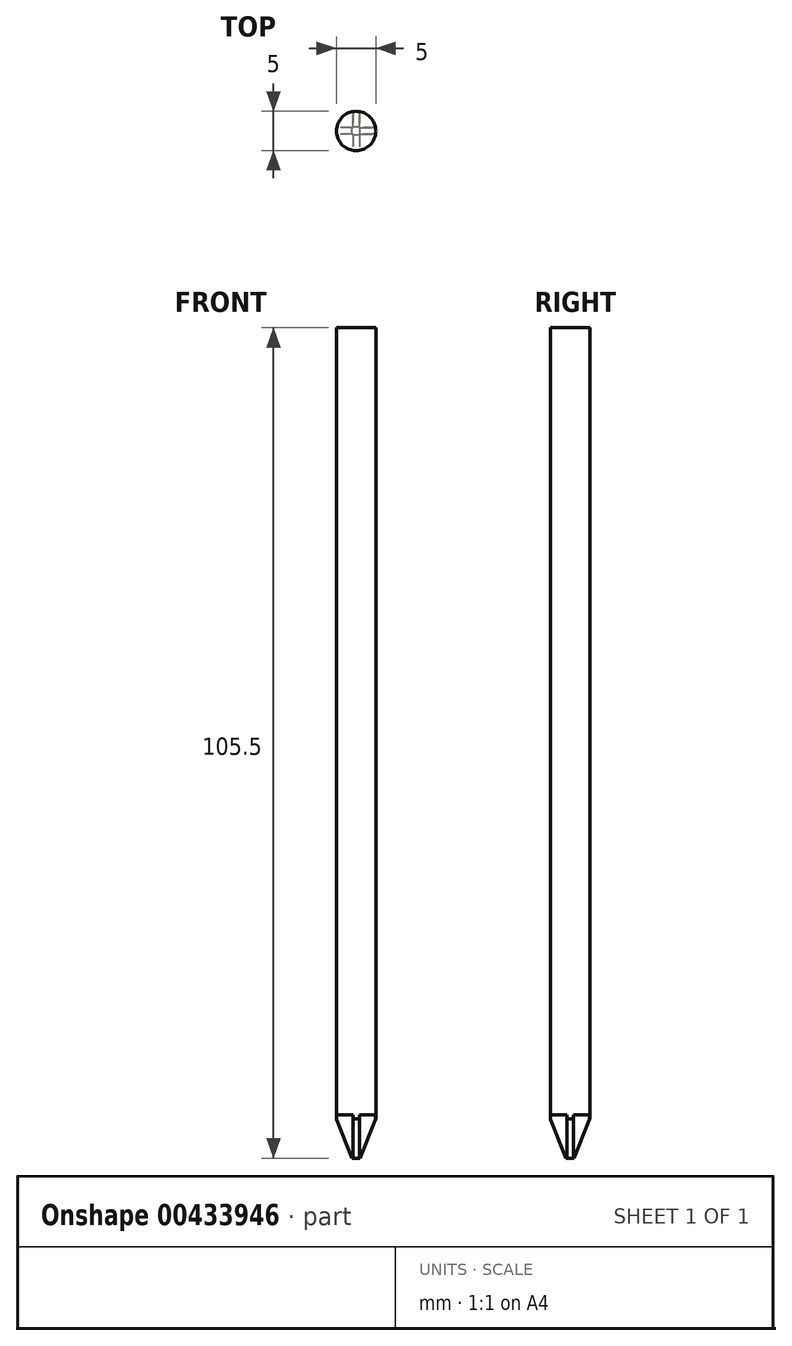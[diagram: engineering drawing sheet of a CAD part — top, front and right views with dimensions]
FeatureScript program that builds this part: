
annotation { "Feature Type Name" : "Feature", "Feature Type Description" : "" }
export const myFeature = defineFeature(function(context is Context, id is Id, definition is map)
    precondition{}
    {
        {
            var Q0;
            Q0=qCreatedBy(makeId("Front.planeOp"),FACE);
            var sketch = newSketch(context, id + "F0", { "sketchPlane" : qUnion([Q0])});
            skLineSegment(sketch, "E0", {"start": v(0, 0) * mm, "end": v(-10, 0) * mm});
            skLineSegment(sketch, "E1", {"start": v(-10, 0) * mm, "end": v(-10, 5) * mm});
            skLineSegment(sketch, "E2", {"start": v(-2.5, 0) * mm, "end": v(-2.5, -100) * mm});
            skLineSegment(sketch, "E3", {"start": v(-2.5, -100) * mm, "end": v(0, -100) * mm});
            skLineSegment(sketch, "E4", {"start": v(0, -100) * mm, "end": v(0, 80) * mm});
            skArc(sketch, "E5", {"start": v(0, 80) * mm, "mid": v(-5.14, 78.95) * mm, "end": v(-10, 77) * mm});
            skArc(sketch, "E6", {"start": v(-10, 5) * mm, "mid": v(-7.2, 7.32) * mm, "end": v(-5.04, 10.25) * mm});
            skArc(sketch, "E7", {"start": v(-10, 77) * mm, "mid": v(-10.59, 43.4) * mm, "end": v(-5.04, 10.25) * mm});
            skSolve(sketch);
        }
        {
            var Q0;
            {var subQ0=sQuery(id+"F0.wireOp",EDGE,"E1");Q0=makeQuery(id+"F0.imprint","IMPRINT",FACE,{"disambiguationData":[TD([[makeQuery(id+"F0.imprint","IMPRINT",EDGE,{"derivedFrom":subQ0}),-1.0]])]});}
            var Q1;
            Q1=sQuery(id+"F0.wireOp",EDGE,"E4");
            revolve(context, id + "F1", {"entities" : qUnion([Q0]), "axis" : qUnion([Q1]), "revolveType" : RevolveType.FULL});
        }
        {
            var Q0;
            {var subQ3=sQuery(id+"F0.wireOp",EDGE,"E2");Q0=makeQuery(id+"F0.imprint","IMPRINT",FACE,{"disambiguationData":[TD([[makeQuery(id+"F0.imprint","IMPRINT",EDGE,{"derivedFrom":subQ3}),1.0]])]});}
            var Q1;
            Q1=sQuery(id+"F0.wireOp",EDGE,"E4");
            revolve(context, id + "F2", {"entities" : qUnion([Q0]), "axis" : qUnion([Q1]), "revolveType" : RevolveType.FULL});
        }
        {
            var Q0;
            Q0=qCreatedBy(makeId("Front.planeOp"),FACE);
            var sketch = newSketch(context, id + "F3", { "sketchPlane" : qUnion([Q0])});
            skLineSegment(sketch, "E8", {"start": v(0, -100) * mm, "end": v(0.5, -100) * mm});
            skLineSegment(sketch, "E9", {"start": v(0.5, -100) * mm, "end": v(2.77, -94.3) * mm});
            skLineSegment(sketch, "E10", {"start": v(2.77, -94.3) * mm, "end": v(0, -94.3) * mm});
            skLineSegment(sketch, "E11", {"start": v(0, -94.3) * mm, "end": v(0, -100) * mm});
            skLineSegment(sketch, "E12.MirrorCS", {"start": v(-2.77, -94.3) * mm, "end": v(0, -94.3) * mm});
            skLineSegment(sketch, "E13.MirrorCS", {"start": v(-0.5, -100) * mm, "end": v(-2.77, -94.3) * mm});
            skLineSegment(sketch, "E14.MirrorCS", {"start": v(0, -100) * mm, "end": v(-0.5, -100) * mm});
            skSolve(sketch);
        }
        {
            var Q0;
            Q0 = qSketchRegion(id + "F3", true);
            extrude(context, id + "F4", {"entities" : qUnion([Q0]), "endBound" : BoundingType.SYMMETRIC, "depth" : 0.8 * mm});
        }
        {
            var Q0;
            Q0=makeQuery(id+"F4.opExtrude","SWEPT_BODY",BODY,{"disambiguationData":[OSD([sQuery(id+"F3.wireOp",EDGE,"E8"),sQuery(id+"F3.wireOp",EDGE,"E9"),sQuery(id+"F3.wireOp",EDGE,"E10"),sQuery(id+"F3.wireOp",EDGE,"E12.MirrorCS"),sQuery(id+"F3.wireOp",EDGE,"E13.MirrorCS"),sQuery(id+"F3.wireOp",EDGE,"E14.MirrorCS")])]});
            var Q1;
            Q1=makeQuery(id+"F2.opRevolve","SWEPT_EDGE",EDGE,{"disambiguationData":[OSD([sQuery(id+"F0.wireOp",EDGE,"E2"),sQuery(id+"F0.wireOp",EDGE,"E3")])]});
            circularPattern(context, id + "F5", {"operationType" : NewBodyOperationType.INTERSECT, "entities" : qUnion([Q0]), "axis" : qUnion([Q1]), "angle" : 90 * degree, "instanceCount" : 2, "isCentered" : true});
        }
        {
            var Q0;
            Q0=makeQuery(id+"F2.opRevolve","SWEPT_BODY",BODY,{"disambiguationData":[OSD([sQuery(id+"F0.wireOp",EDGE,"E0"),sQuery(id+"F0.wireOp",EDGE,"E2"),sQuery(id+"F0.wireOp",EDGE,"E3"),sQuery(id+"F0.wireOp",EDGE,"E4")])]});
            var Q1;
            Q1=sQuery(id+"F0.wireOp",EDGE,"E3");
            var Q2;
            Q2=sQuery(id+"F0.wireOp",EDGE,"E4");
            transform(context, id + "F6", {"entities" : qUnion([Q0]), "transformType" : TransformType.TRANSLATION_DISTANCE, "transformDirection" : qUnion([Q2]), "distance" : 5.5 * mm, "oppositeDirection" : true, "makeCopy" : false});
        }
        {
            var Q0;
            {var subQ3=sQuery(id+"F0.wireOp",EDGE,"E2");Q0=makeQuery(id+"F0.imprint","IMPRINT",FACE,{"disambiguationData":[TD([[makeQuery(id+"F0.imprint","IMPRINT",EDGE,{"derivedFrom":subQ3}),1.0]])]});}
            var Q1;
            Q1=sQuery(id+"F0.wireOp",EDGE,"E4");
            revolve(context, id + "F7", {"operationType" : NewBodyOperationType.ADD, "entities" : qUnion([Q0]), "axis" : qUnion([Q1]), "revolveType" : RevolveType.FULL});
        }
    });
